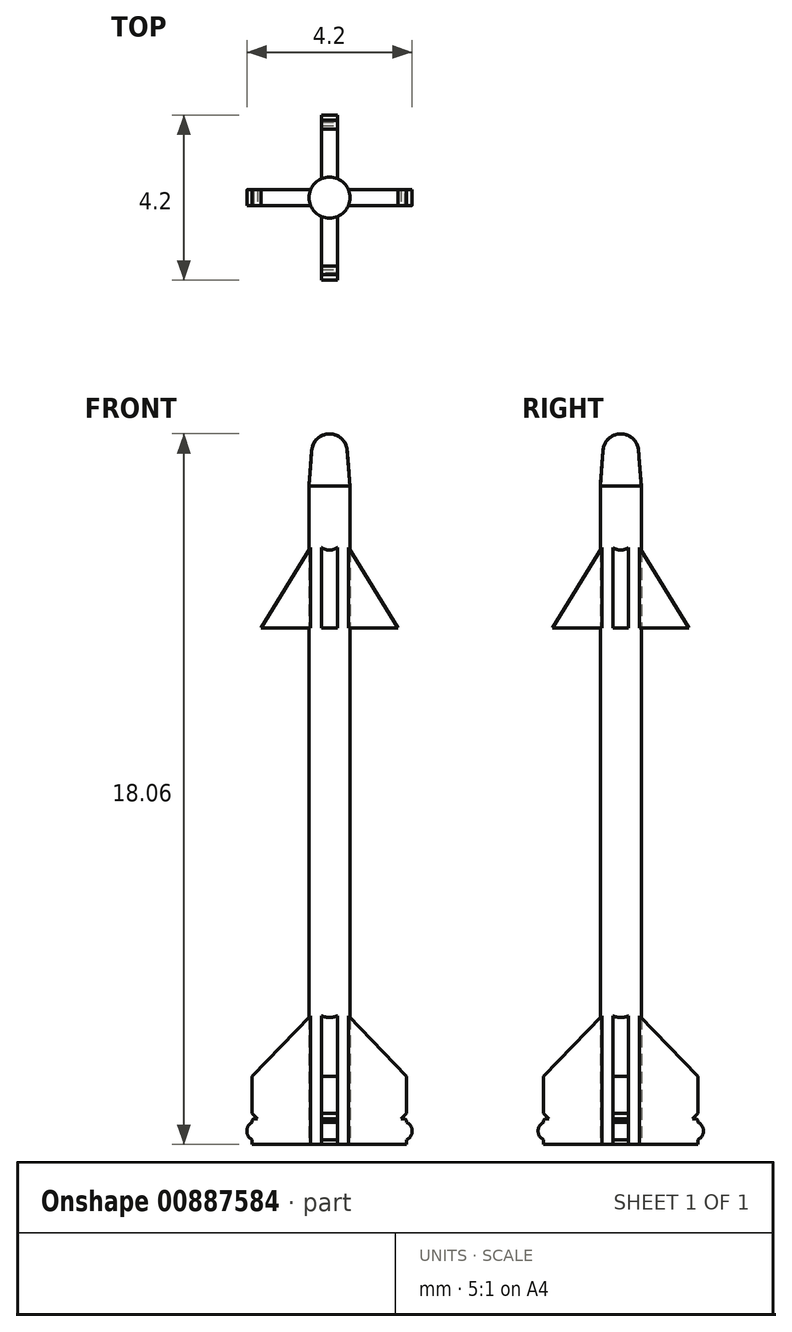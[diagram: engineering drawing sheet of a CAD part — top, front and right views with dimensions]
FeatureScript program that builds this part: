
annotation { "Feature Type Name" : "Feature", "Feature Type Description" : "" }
export const myFeature = defineFeature(function(context is Context, id is Id, definition is map)
    precondition{}
    {
        {
            var Q0;
            Q0=qCreatedBy(makeId("Front.planeOp"),FACE);
            var sketch = newSketch(context, id + "F0", { "sketchPlane" : qUnion([Q0])});
            skLineSegment(sketch, "E0", {"start": v(0, 0) * mm, "end": v(0, 18.06) * mm});
            skLineSegment(sketch, "E1", {"start": v(0.52, 16.74) * mm, "end": v(0.52, 0) * mm});
            skLineSegment(sketch, "E2", {"start": v(0.52, 0) * mm, "end": v(0, 0) * mm});
            skLineSegment(sketch, "E3", {"start": v(0, 18.06) * mm, "end": v(1.85, 18.06) * mm, "construction": true});
            skLineSegment(sketch, "E4", {"start": v(0.52, 16.74) * mm, "end": v(0.45, 17.64) * mm});
            skArc(sketch, "E5", {"start": v(0.45, 17.64) * mm, "mid": v(0.3, 17.94) * mm, "end": v(0, 18.06) * mm});
            skSolve(sketch);
        }
        {
            var Q0;
            Q0=qSketchRegion(id+"F0",true);
            var Q1;
            Q1=sQuery(id+"F0.wireOp",EDGE,"E0");
            revolve(context, id + "F1", {"surfaceOperationType" : NewSurfaceOperationType.NEW, "entities" : qUnion([Q0]), "axis" : qUnion([Q1]), "revolveType" : RevolveType.FULL});
        }
        {
            var Q0;
            Q0=qCreatedBy(makeId("Front.planeOp"),FACE);
            var sketch = newSketch(context, id + "F2", { "sketchPlane" : qUnion([Q0])});
            skLineSegment(sketch, "E6", {"start": v(0.33, 3.43) * mm, "end": v(-0.33, 3.43) * mm});
            skLineSegment(sketch, "E7", {"start": v(-1.96, 1.74) * mm, "end": v(-0.33, 3.43) * mm});
            skLineSegment(sketch, "E8", {"start": v(-1.96, 1.74) * mm, "end": v(-1.96, 0.8) * mm});
            skLineSegment(sketch, "E9", {"start": v(-1.96, 0) * mm, "end": v(1.96, 0) * mm});
            skLineSegment(sketch, "E10", {"start": v(1.96, 0.8) * mm, "end": v(1.96, 1.74) * mm});
            skLineSegment(sketch, "E11", {"start": v(0.33, 3.43) * mm, "end": v(1.96, 1.74) * mm});
            skLineSegment(sketch, "E12", {"start": v(0, 0) * mm, "end": v(0, 3.43) * mm, "construction": true});
            skLineSegment(sketch, "E13", {"start": v(-0.52, 0) * mm, "end": v(-0.52, 4.16) * mm, "construction": true});
            skLineSegment(sketch, "E14.0", {"start": v(0.52, 16.74) * mm, "end": v(-0.52, 16.74) * mm});
            skPoint(sketch, "E15", {"position": v(-0.52, 3.23) * mm});
            skLineSegment(sketch, "E16", {"start": v(-1.96, 0) * mm, "end": v(-1.96, 0.12) * mm});
            skLineSegment(sketch, "E17", {"start": v(1.96, 0) * mm, "end": v(1.96, 0.12) * mm});
            skLineSegment(sketch, "E18", {"start": v(1.96, 0.8) * mm, "end": v(1.82, 0.66) * mm});
            skLineSegment(sketch, "E19", {"start": v(1.96, 0.61) * mm, "end": v(1.96, 0.56) * mm});
            skLineSegment(sketch, "E20", {"start": v(-1.96, 0.8) * mm, "end": v(-1.82, 0.66) * mm});
            skLineSegment(sketch, "E21", {"start": v(-1.96, 0.62) * mm, "end": v(-1.96, 0.56) * mm});
            skArc(sketch, "E22", {"start": v(-1.96, 0.56) * mm, "mid": v(-2.1, 0.34) * mm, "end": v(-1.96, 0.13) * mm});
            skArc(sketch, "E23", {"start": v(1.96, 0.13) * mm, "mid": v(2.1, 0.34) * mm, "end": v(1.96, 0.56) * mm});
            skLineSegment(sketch, "E24", {"start": v(-1.96, 0.62) * mm, "end": v(-1.92, 0.66) * mm});
            skLineSegment(sketch, "E25", {"start": v(-1.92, 0.66) * mm, "end": v(-1.82, 0.66) * mm});
            skLineSegment(sketch, "E26", {"start": v(1.96, 0.61) * mm, "end": v(1.93, 0.66) * mm});
            skLineSegment(sketch, "E27", {"start": v(1.93, 0.66) * mm, "end": v(1.82, 0.66) * mm});
            skLineSegment(sketch, "E28", {"start": v(-0.34, 15.4) * mm, "end": v(-1.74, 13.12) * mm});
            skLineSegment(sketch, "E29", {"start": v(-1.74, 13.12) * mm, "end": v(1.74, 13.12) * mm});
            skLineSegment(sketch, "E30", {"start": v(1.74, 13.12) * mm, "end": v(0.34, 15.4) * mm});
            skLineSegment(sketch, "E31", {"start": v(0.34, 15.4) * mm, "end": v(-0.34, 15.4) * mm});
            skLineSegment(sketch, "E32", {"start": v(0, 13.12) * mm, "end": v(0, 0) * mm, "construction": true});
            skLineSegment(sketch, "E33", {"start": v(-0.52, 16.74) * mm, "end": v(-0.52, 14.02) * mm, "construction": true});
            skPoint(sketch, "E34", {"position": v(-0.52, 15.1) * mm});
            skSolve(sketch);
        }
        {
            var Q0;
            Q0=qSketchRegion(id+"F2",true);
            extrude(context, id + "F3", {"entities" : qUnion([Q0]), "operationType" : NewBodyOperationType.ADD, "depth" : .4 * mm, "offsetDistance" : 25 * mm, "symmetric" : true});
        }
        {
            var Q0;
            Q0=makeQuery(id+"F1.opRevolve","SWEPT_BODY",BODY,{"disambiguationData":[OSD([sQuery(id+"F0.wireOp",EDGE,"E0"),sQuery(id+"F0.wireOp",EDGE,"E1"),sQuery(id+"F0.wireOp",EDGE,"E2"),sQuery(id+"F0.wireOp",EDGE,"m1K1lCZm-MTc8-Btmt-IA6e-LtdyprMEJuD3")])]});
            var Q1;
            Q1=makeQuery(id+"F1.opRevolve","SWEPT_FACE",FACE,{"disambiguationData":[OSD([sQuery(id+"F0.wireOp",EDGE,"E1")])]});
            circularPattern(context, id + "F4", {"entities" : qUnion([Q0]), "axis" : qUnion([Q1]), "angle" : 360 * degree, "instanceCount" : 4, "equalSpace" : true, "computeTransformsWithoutBuiltin" : true});
        }
    });
